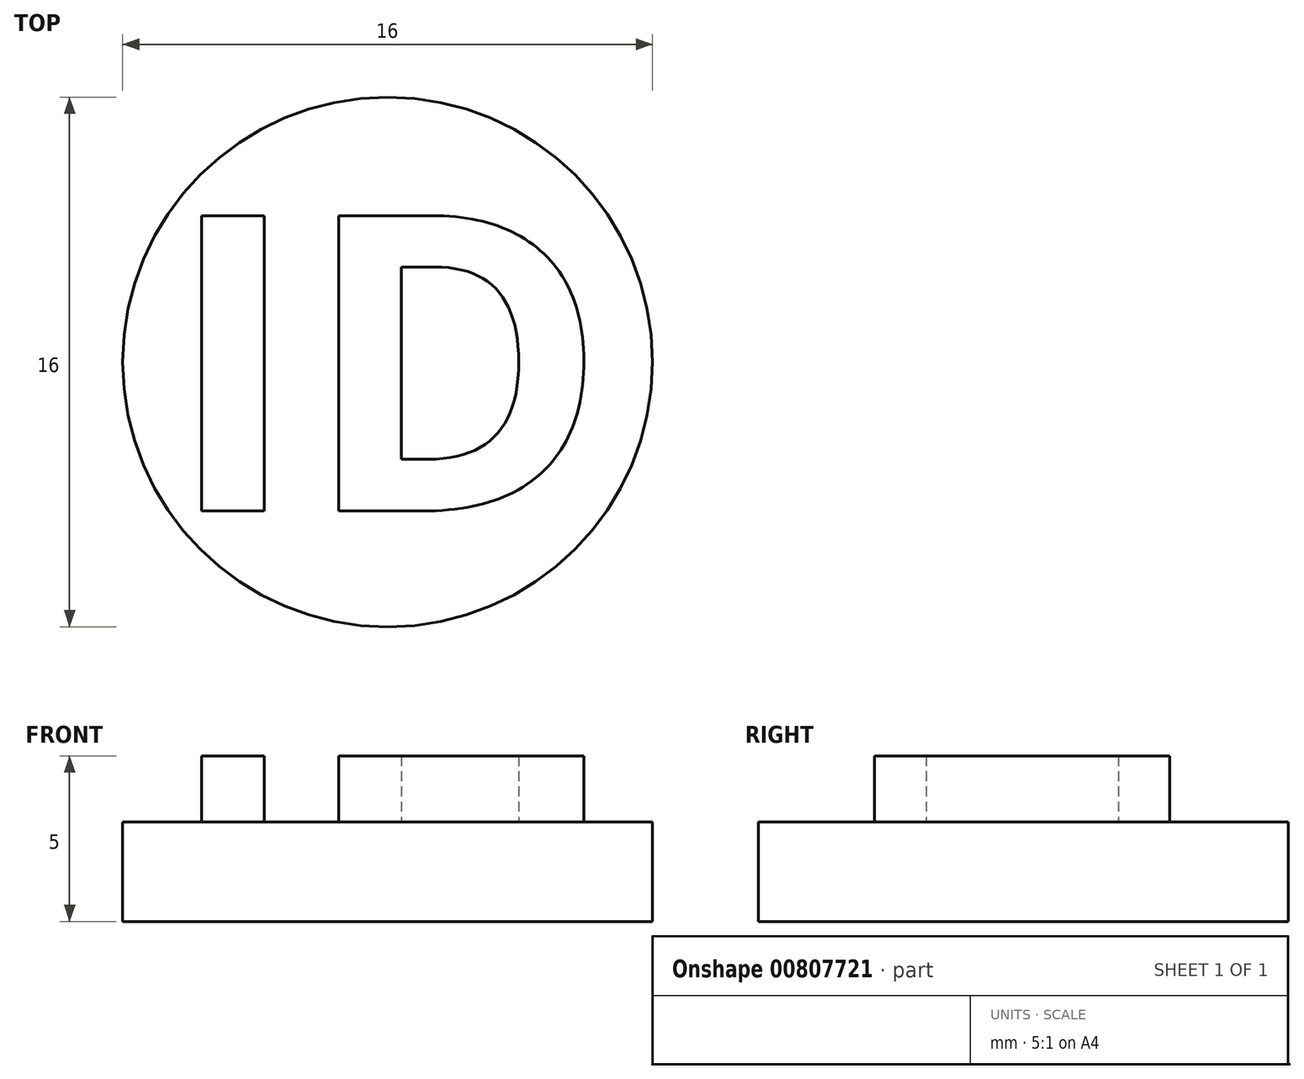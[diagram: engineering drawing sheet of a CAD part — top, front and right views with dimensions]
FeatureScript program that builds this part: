
annotation { "Feature Type Name" : "Feature", "Feature Type Description" : "" }
export const myFeature = defineFeature(function(context is Context, id is Id, definition is map)
    precondition{}
    {
        {
            var Q0;
            Q0=qCreatedBy(makeId("Top.planeOp"),FACE);
            var sketch = newSketch(context, id + "F0", { "sketchPlane" : qUnion([Q0])});
            skCircle(sketch, "E0", {"center": v(0, 0) * mm, "radius": 8 * mm});
            skText(sketch, "E1", { "text": "ID", "fontName": "OpenSans-Bold.ttf"});
            const initialGuessF0  = {"E1": [-0.00674, -0.0045, 1, 0, 0.009]};
            skSetInitialGuess(sketch, initialGuessF0);
            skSolve(sketch);
        }
        {
            var Q0;
            Q0=makeQuery(id+"F0.imprint","IMPRINT",FACE,{"disambiguationData":[TD([[makeQuery(id+"F0.imprint","IMPRINT",EDGE,{"derivedFrom":sQuery(id+"F0.wireOp",EDGE,"E0")}),1.0]])]});
            var Q1;
            Q1=makeQuery(id+"F0.imprint","IMPRINT",FACE,{"disambiguationData":[TD([[makeQuery(id+"F0.imprint","IMPRINT",EDGE,{"derivedFrom":sQuery(id+"F0.wireOp",EDGE,"E1.sketch_text.stroke-11")}),1.0]])]});
            extrude(context, id + "F1", {"entities" : qUnion([Q0, Q1]), "depth" : 3 * mm, "offsetDistance" : 25 * mm});
        }
        {
            var Q0;
            Q0=makeQuery(id+"F0.imprint","IMPRINT",FACE,{"disambiguationData":[TD([[makeQuery(id+"F0.imprint","IMPRINT",EDGE,{"derivedFrom":sQuery(id+"F0.wireOp",EDGE,"E1.sketch_text.stroke-0")}),-1.0]])]});
            var Q1;
            Q1=makeQuery(id+"F0.imprint","IMPRINT",FACE,{"disambiguationData":[TD([[makeQuery(id+"F0.imprint","IMPRINT",EDGE,{"derivedFrom":sQuery(id+"F0.wireOp",EDGE,"E1.sketch_text.stroke-4")}),-1.0]])]});
            extrude(context, id + "F2", {"entities" : qUnion([Q0, Q1]), "operationType" : NewBodyOperationType.ADD, "depth" : 5 * mm, "offsetDistance" : 25 * mm});
        }
    });
